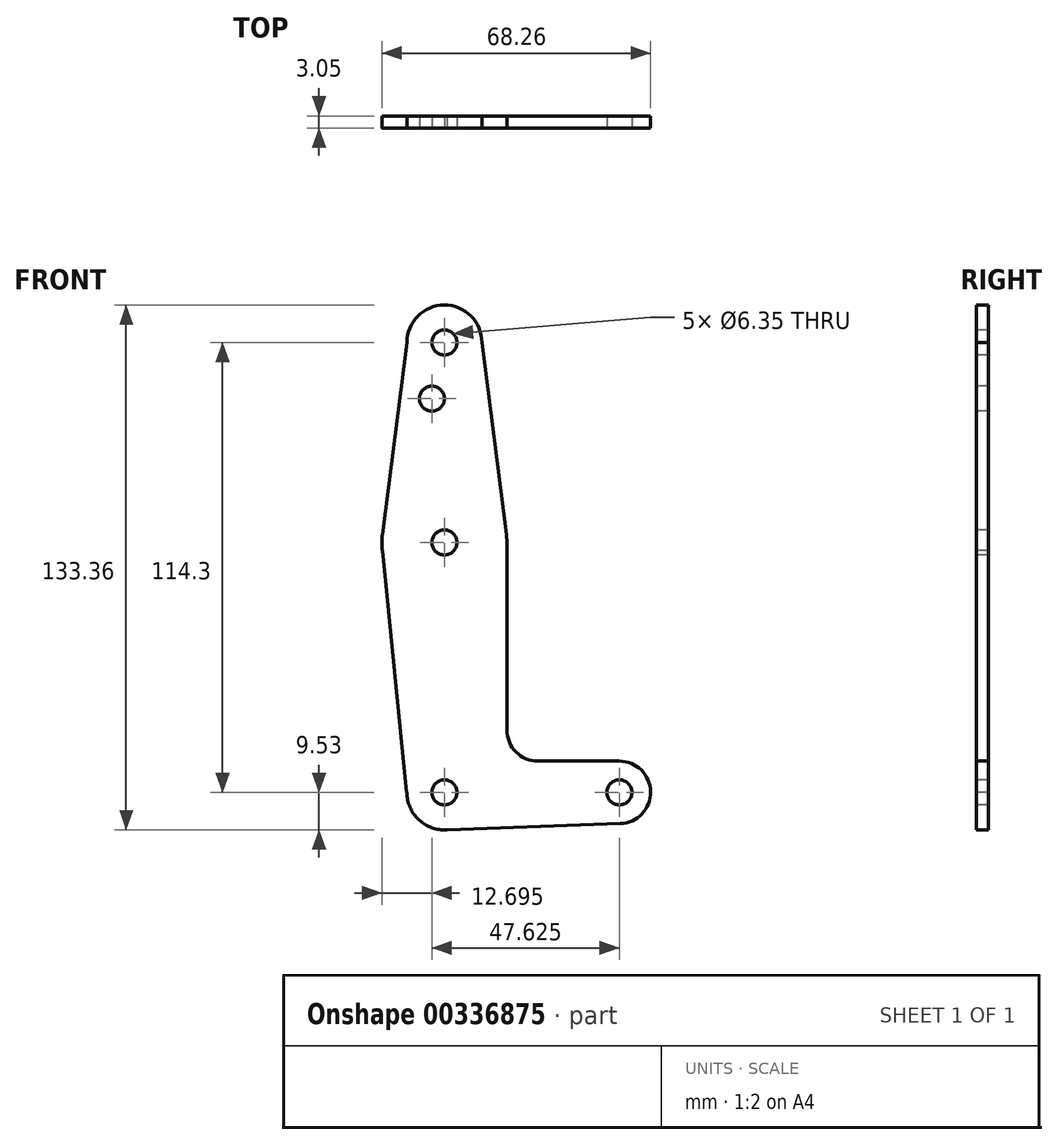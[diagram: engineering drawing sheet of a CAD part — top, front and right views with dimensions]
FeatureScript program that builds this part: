
annotation { "Feature Type Name" : "Feature", "Feature Type Description" : "" }
export const myFeature = defineFeature(function(context is Context, id is Id, definition is map)
    precondition{}
    {
        {
            var Q0;
            Q0=qCreatedBy(makeId("Front.planeOp"),FACE);
            var sketch = newSketch(context, id + "F0", { "sketchPlane" : qUnion([Q0])});
            skLineSegment(sketch, "E0", {"start": v(0, 0) * mm, "end": v(0, 114.3) * mm, "construction": true});
            skLineSegment(sketch, "E1", {"start": v(0, 0) * mm, "end": v(44.45, 0) * mm, "construction": true});
            skCircle(sketch, "E2", {"center": v(44.45, 0) * mm, "radius": 7.94 * mm});
            skCircle(sketch, "E3", {"center": v(0, 0) * mm, "radius": 9.53 * mm});
            skCircle(sketch, "E4", {"center": v(0, 114.3) * mm, "radius": 9.53 * mm});
            skCircle(sketch, "E5", {"center": v(0, 63.5) * mm, "radius": 15.88 * mm});
            skLineSegment(sketch, "E6", {"start": v(0, 0) * mm, "end": v(-22.28, 0) * mm});
            skLineSegment(sketch, "E7", {"start": v(9.52, 114.3) * mm, "end": v(15.75, 65.5) * mm});
            skLineSegment(sketch, "E8", {"start": v(23.83, 7.94) * mm, "end": v(44.45, 7.94) * mm});
            skLineSegment(sketch, "E9", {"start": v(0, -9.53) * mm, "end": v(44.73, -7.93) * mm});
            skLineSegment(sketch, "E10", {"start": v(-9.53, 114.3) * mm, "end": v(-15.75, 65.5) * mm});
            skLineSegment(sketch, "E11", {"start": v(-15.75, 61.5) * mm, "end": v(-9.57, 0) * mm});
            skLineSegment(sketch, "E12", {"start": v(15.88, 15.89) * mm, "end": v(15.88, 63.5) * mm});
            skCircle(sketch, "E13", {"center": v(0, 114.3) * mm, "radius": 3.18 * mm});
            skCircle(sketch, "E14", {"center": v(0, 63.5) * mm, "radius": 3.18 * mm});
            skCircle(sketch, "E15", {"center": v(44.45, 0) * mm, "radius": 3.18 * mm});
            skCircle(sketch, "E16", {"center": v(0, 0) * mm, "radius": 3.18 * mm});
            skCircle(sketch, "E17", {"center": v(-3.18, 100.03) * mm, "radius": 3.18 * mm});
            skArc(sketch, "E18.filletArc", {"start": v(15.88, 15.89) * mm, "mid": v(18.2, 10.27) * mm, "end": v(23.83, 7.94) * mm});
            skLineSegment(sketch, "E19", {"start": v(-3.18, 100.03) * mm, "end": v(-3.18, 96.85) * mm});
            skSolve(sketch);
        }
        {
            var Q0;
            Q0 = qSketchRegion(id + "F0", true);
            extrude(context, id + "F1", {"entities" : qUnion([Q0]), "oppositeDirection" : true, "depth" : 3.05 * mm});
        }
    });
